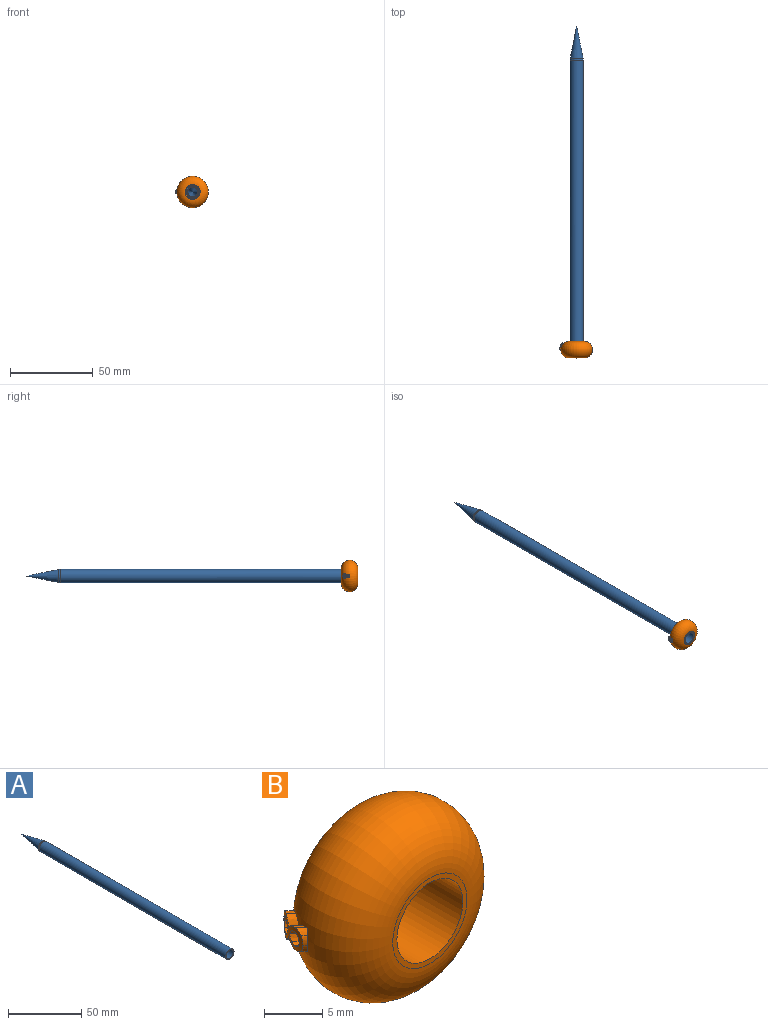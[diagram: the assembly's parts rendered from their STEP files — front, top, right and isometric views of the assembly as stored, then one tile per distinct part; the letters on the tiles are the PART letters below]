
ASSEMBLY  parts=2 mates=1
PART A: 8 faces, bbox 8x200x8 mm
  f0: cylinder r=3.5mm len=180mm, axis (0,1,0), area 3958.4mm2, adj f2,f4
  f1: cylinder r=4mm len=179.51mm, axis (0,1,0), area 4511.5mm2, adj f2,f5
  f2: plane 8x8mm, normal (0,-1,0), area 11.8mm2, adj f0,f1
  f3: cone r=4mm half-angle=11.3deg, axis (0,-1,0), area 244mm2, adj f5
  f4: plane 7x7mm, normal (0,-1,0), area 10.8mm2, adj f0,f6
  f5: revolved ~8x8mm, area 24.6mm2, adj f1,f3
  f6: revolved ~5.94x5.94mm, area 5.4mm2, adj f4,f7
  f7: cone r=3.02mm half-angle=11.3deg, axis (0,-1,0), area 136.8mm2, adj f6
PART B: 38 faces, bbox 20.1x10x14.5 mm
  f0: plane 2.31x0.66mm, normal (0.71,-0.71,0), area 1mm2, adj f1,f2,f3,f8,f20,f21,f22,f23
  f1: extruded ~1.2x1.2mm, area 0.6mm2, adj f0,f19,f22,f32,f34
  f2: extruded ~1.07x1.07mm, area 0.5mm2, adj f0,f7,f20,f32,f34
  f3: extruded ~1.07x1.07mm, area 0.4mm2, adj f0,f4,f21,f32,f34
  f4: extruded ~1.17x1.17mm, area 0.4mm2, adj f3,f5,f32,f34
  f5: extruded ~1.03x1.03mm, area 0.6mm2, adj f4,f6,f32,f34
  f6: extruded ~1.02x1.02mm, area 0.6mm2, adj f5,f7,f32,f34
  f7: extruded ~1.18x1.18mm, area 0.4mm2, adj f2,f6,f32,f34
  f8: extruded ~1.22x1.22mm, area 0.6mm2, adj f0,f9,f23,f32,f34
  f9: extruded ~1.3x1.3mm, area 0.5mm2, adj f8,f10,f32,f34
  f10: extruded ~1.12x1.12mm, area 0.6mm2, adj f9,f11,f32,f34
  f11: extruded ~1.04x1.04mm, area 0.7mm2, adj f10,f12,f32,f34
  f12: extruded ~1.09x1.09mm, area 0.5mm2, adj f11,f13,f32,f34
  f13: extruded ~1.22x1.22mm, area 0.7mm2, adj f12,f14,f32,f34
  f14: extruded ~0.93x0.8mm, area 0.8mm2, adj f13,f15,f32,f34
  f15: extruded ~0.96x0.8mm, area 0.8mm2, adj f14,f16,f32,f34
  f16: extruded ~1.22x1.22mm, area 0.7mm2, adj f15,f17,f32,f34
  f17: extruded ~1.52x1.52mm, area 1.2mm2, adj f16,f18,f32,f34
  f18: extruded ~1.14x1.14mm, area 0.6mm2, adj f17,f19,f32,f34
  f19: extruded ~1.31x1.31mm, area 0.5mm2, adj f1,f18,f32,f34
  f20: extruded ~0.68x0.68mm, area 0.4mm2, adj f0,f2,f21,f32
  f21: extruded ~0.68x0.68mm, area 0.4mm2, adj f0,f3,f20,f32
  f22: extruded ~0.84x0.57mm, area 0.4mm2, adj f0,f1,f23,f32
  f23: extruded ~0.84x0.57mm, area 0.4mm2, adj f0,f8,f22,f32
  f24: extruded ~0.96x0.96mm, area 0.7mm2, adj f25,f31,f32,f33
  f25: extruded ~0.98x0.98mm, area 0.4mm2, adj f24,f26,f32,f33
  f26: extruded ~1x1mm, area 0.5mm2, adj f25,f27,f32,f33
  f27: extruded ~0.72x0.72mm, area 0.5mm2, adj f26,f28,f32,f33
  f28: extruded ~0.72x0.72mm, area 0.5mm2, adj f27,f29,f32,f33
  f29: extruded ~0.99x0.99mm, area 0.5mm2, adj f28,f30,f32,f33
  f30: extruded ~1.01x1.01mm, area 0.4mm2, adj f29,f31,f32,f33
  f31: extruded ~0.94x0.94mm, area 0.6mm2, adj f24,f30,f32,f33
  f32: torus R=4.5mm, axis (0,-1,0), area 5.1mm2, adj f1,f2,f3,f4,f5,f6,f7,f8
  f33: torus R=4.5mm, axis (0,-1,0), area 2mm2, adj f24,f25,f26,f27,f28,f29,f30,f31
  f34: torus R=4.5mm, axis (0,-1,0), area 752.5mm2, adj f0,f1,f2,f3,f4,f5,f6,f7
  f35: cylinder r=4mm len=10mm, axis (0,1,0), area 251.3mm2, adj f36,f37
  f36: plane 9x9mm, normal (0,-1,0), area 13.4mm2, adj f34,f35
  f37: plane 9x9mm, normal (0,1,0), area 13.4mm2, adj f34,f35
PLACE A t=(-8.59,166.17,-5.43)mm
PLACE B t=(-8.59,-3.83,-5.43)mm fixed
MATE fastened A.f0 <-> B.f32  axis (0,-1,0) through (-8.59,-13.83,-5.43)mm
